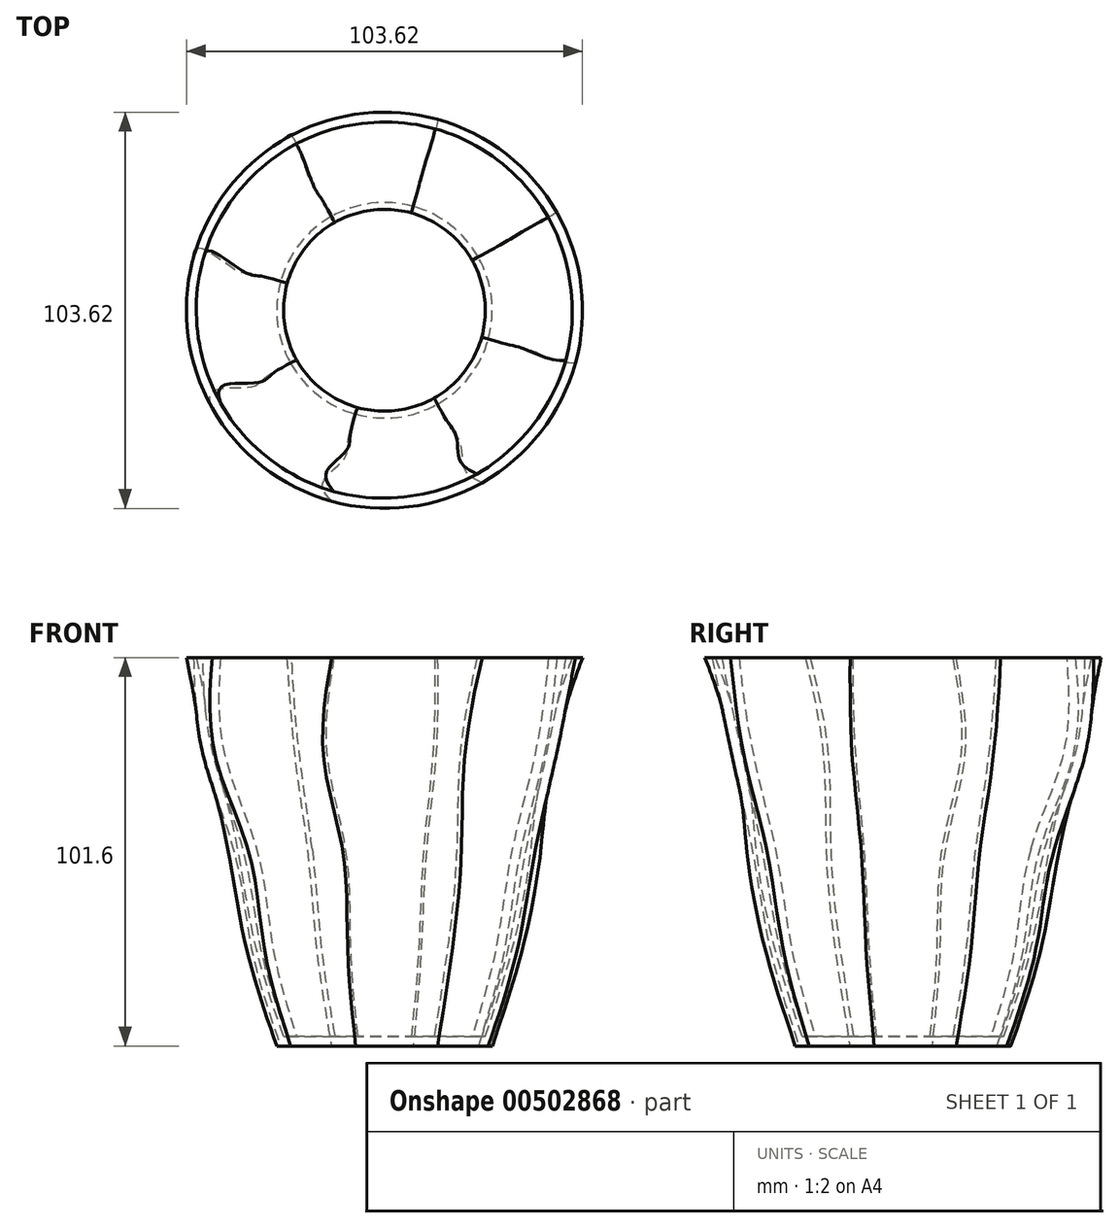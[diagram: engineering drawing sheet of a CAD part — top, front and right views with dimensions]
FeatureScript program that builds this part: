
annotation { "Feature Type Name" : "Feature", "Feature Type Description" : "" }
export const myFeature = defineFeature(function(context is Context, id is Id, definition is map)
    precondition{}
    {
        {
            var Q0;
            Q0=qCreatedBy(makeId("Top.planeOp"),FACE);
            var sketch = newSketch(context, id + "F0", { "sketchPlane" : qUnion([Q0])});
            skCircle(sketch, "E0", {"center": v(0, 0) * mm, "radius": 28.19 * mm});
            skSolve(sketch);
        }
        {
            var Q0;
            Q0=qCreatedBy(makeId("Top.planeOp"),FACE);
            cPlane(context, id + "F1", {"entities" : qUnion([Q0]), "cplaneType" : CPlaneType.OFFSET, "offset" : 25.4 * mm, "width" : 152.4 * mm, "height" : 152.4 * mm});
        }
        {
            var Q0;
            Q0=qCreatedBy(id+"F1.planeOp",FACE);
            var sketch = newSketch(context, id + "F2", { "sketchPlane" : qUnion([Q0])});
            skCircle(sketch, "E1", {"center": v(0, 0) * mm, "radius": 36.08 * mm});
            skSolve(sketch);
        }
        {
            var Q0;
            Q0=qCreatedBy(id+"F1.planeOp",FACE);
            cPlane(context, id + "F3", {"entities" : qUnion([Q0]), "cplaneType" : CPlaneType.OFFSET, "offset" : 25.4 * mm, "width" : 152.4 * mm, "height" : 152.4 * mm});
        }
        {
            var Q0;
            Q0=qCreatedBy(id+"F3.planeOp",FACE);
            var sketch = newSketch(context, id + "F4", { "sketchPlane" : qUnion([Q0])});
            skCircle(sketch, "E2", {"center": v(0, 0) * mm, "radius": 40.83 * mm});
            skSolve(sketch);
        }
        {
            var Q0;
            Q0=qCreatedBy(id+"F3.planeOp",FACE);
            cPlane(context, id + "F5", {"entities" : qUnion([Q0]), "cplaneType" : CPlaneType.OFFSET, "offset" : 25.4 * mm, "width" : 152.4 * mm, "height" : 152.4 * mm});
        }
        {
            var Q0;
            Q0=qCreatedBy(id+"F5.planeOp",FACE);
            var sketch = newSketch(context, id + "F6", { "sketchPlane" : qUnion([Q0])});
            skCircle(sketch, "E3.cCircle", {"center": v(-1.26, 1.41) * mm, "radius": 44.8 * mm, "construction": true});
            skLineSegment(sketch, "E3.0", {"start": v(41.82, 23.68) * mm, "end": v(44.95, -13.3) * mm});
            skLineSegment(sketch, "E3.1", {"start": v(44.95, -13.3) * mm, "end": v(21, -41.66) * mm});
            skLineSegment(sketch, "E3.2", {"start": v(21, -41.66) * mm, "end": v(-15.98, -44.8) * mm});
            skLineSegment(sketch, "E3.3", {"start": v(-15.98, -44.8) * mm, "end": v(-44.34, -20.85) * mm});
            skLineSegment(sketch, "E3.4", {"start": v(-44.34, -20.85) * mm, "end": v(-47.46, 16.13) * mm});
            skLineSegment(sketch, "E3.5", {"start": v(-47.46, 16.13) * mm, "end": v(-23.52, 44.5) * mm});
            skLineSegment(sketch, "E3.6", {"start": v(-23.52, 44.5) * mm, "end": v(13.46, 47.62) * mm});
            skLineSegment(sketch, "E3.7", {"start": v(13.46, 47.62) * mm, "end": v(41.82, 23.68) * mm});
            skPoint(sketch, "E3.0.midPoint", {"position": v(43.38, 5.19) * mm});
            skSolve(sketch);
        }
        {
            var Q0;
            Q0=qCreatedBy(id+"F5.planeOp",FACE);
            cPlane(context, id + "F7", {"entities" : qUnion([Q0]), "cplaneType" : CPlaneType.OFFSET, "offset" : 25.4 * mm, "width" : 152.4 * mm, "height" : 152.4 * mm});
        }
        {
            var Q0;
            Q0=qCreatedBy(id+"F7.planeOp",FACE);
            var sketch = newSketch(context, id + "F8", { "sketchPlane" : qUnion([Q0])});
            skCircle(sketch, "E4", {"center": v(0, 0) * mm, "radius": 51.81 * mm});
            skSolve(sketch);
        }
        {
            var Q0;
            Q0=makeQuery(id+"F8.imprint","IMPRINT",FACE,{"disambiguationData":[TD([[makeQuery(id+"F8.imprint","IMPRINT",EDGE,{"derivedFrom":sQuery(id+"F8.wireOp",EDGE,"E4")}),1.0]])]});
            var Q1;
            Q1=makeQuery(id+"F6.imprint","IMPRINT",FACE,{"disambiguationData":[TD([[makeQuery(id+"F6.imprint","IMPRINT",EDGE,{"derivedFrom":sQuery(id+"F6.wireOp",EDGE,"E3.0")}),-1.0]])]});
            var Q2;
            Q2=makeQuery(id+"F4.imprint","IMPRINT",FACE,{"disambiguationData":[TD([[makeQuery(id+"F4.imprint","IMPRINT",EDGE,{"derivedFrom":sQuery(id+"F4.wireOp",EDGE,"E2")}),1.0]])]});
            var Q3;
            Q3=makeQuery(id+"F2.imprint","IMPRINT",FACE,{"disambiguationData":[TD([[makeQuery(id+"F2.imprint","IMPRINT",EDGE,{"derivedFrom":sQuery(id+"F2.wireOp",EDGE,"E1")}),1.0]])]});
            var Q4;
            Q4=makeQuery(id+"F0.imprint","IMPRINT",FACE,{"disambiguationData":[TD([[makeQuery(id+"F0.imprint","IMPRINT",EDGE,{"derivedFrom":sQuery(id+"F0.wireOp",EDGE,"E0")}),1.0]])]});
            loft(context, id + "F9", {"sheetProfilesArray" : [{ "sheetProfileEntities" : qUnion([Q0]) }, { "sheetProfileEntities" : qUnion([Q1]) }, { "sheetProfileEntities" : qUnion([Q2]) }, { "sheetProfileEntities" : qUnion([Q3]) }, { "sheetProfileEntities" : qUnion([Q4]) }]});
        }
        {
            var Q0;
            Q0=makeQuery(id+"F9.opLoft","CAP_FACE",FACE,{"disambiguationData":[OSD([makeQuery(id+"F8.imprint","IMPRINT",FACE,{"disambiguationData":[TD([[makeQuery(id+"F8.imprint","IMPRINT",EDGE,{"derivedFrom":sQuery(id+"F8.wireOp",EDGE,"E4")}),1.0]])]})])],"isStart":true});
            shell(context, id + "F10", {"entities" : qUnion([Q0]), "thickness" : 2.54 * mm});
        }
    });
